# Revit family: Claraboya
name_source: partatom
category: Ventanas
units: mm (PartAtom-declared; Revit-internal decimal feet)

## family parameters
Anfitrión = Cubierta
Compartido = No
Corte con vacíos al cargar = No
Punto de cálculo de habitación = No
Siempre vertical = No

## types (8) — shared parameters
Coeficiente de incremento de calor solar = 0.78
Coeficiente de transferencia de calor (U) = 3.6886 W/(m²·K)
Construcción analítica = 1/8 en cristalera simple Pilkington
Definir propiedades térmicas por = Tipo esquemático
ID de tipo de construcción = GSP4R
Material de estructura = Metal - Bronce, Bruñido ligero
Material de hoja = Metal - Bronce, Bruñido ligero
Material de hoja de cristal = Vidrio
Resistencia térmica (R) = 0.2711 (m²·K)/W
Transmitancia de luz visual = 0.9

## per-type parameters (varying)
| type | Altura | Anchura |
| 0711 x 0965mm | 965 mm | 711 mm |
| 0610 x 0686mm | 686 mm  [stored 2.25066 ft] | 610 mm  [stored 2.00131 ft] |
| 0406 x 1170mm | 1170 mm | 406 mm  [stored 1.33202 ft] |
| 1180 x 1170mm | 1170 mm | 1118 mm  [stored 3.66798 ft] |
| 0711 x 1830mm | 1830 mm | 711 mm |
| 240 x 100 cm | 2400 mm | 1000 mm |
| 100 x 100 cm | 1000 mm | 1000 mm |
| 140 x 100 cm | 1400 mm | 1000 mm |

note: [stored X ft] marks values corroborated as IEEE doubles in the binary element streams (Revit-internal decimal feet)
